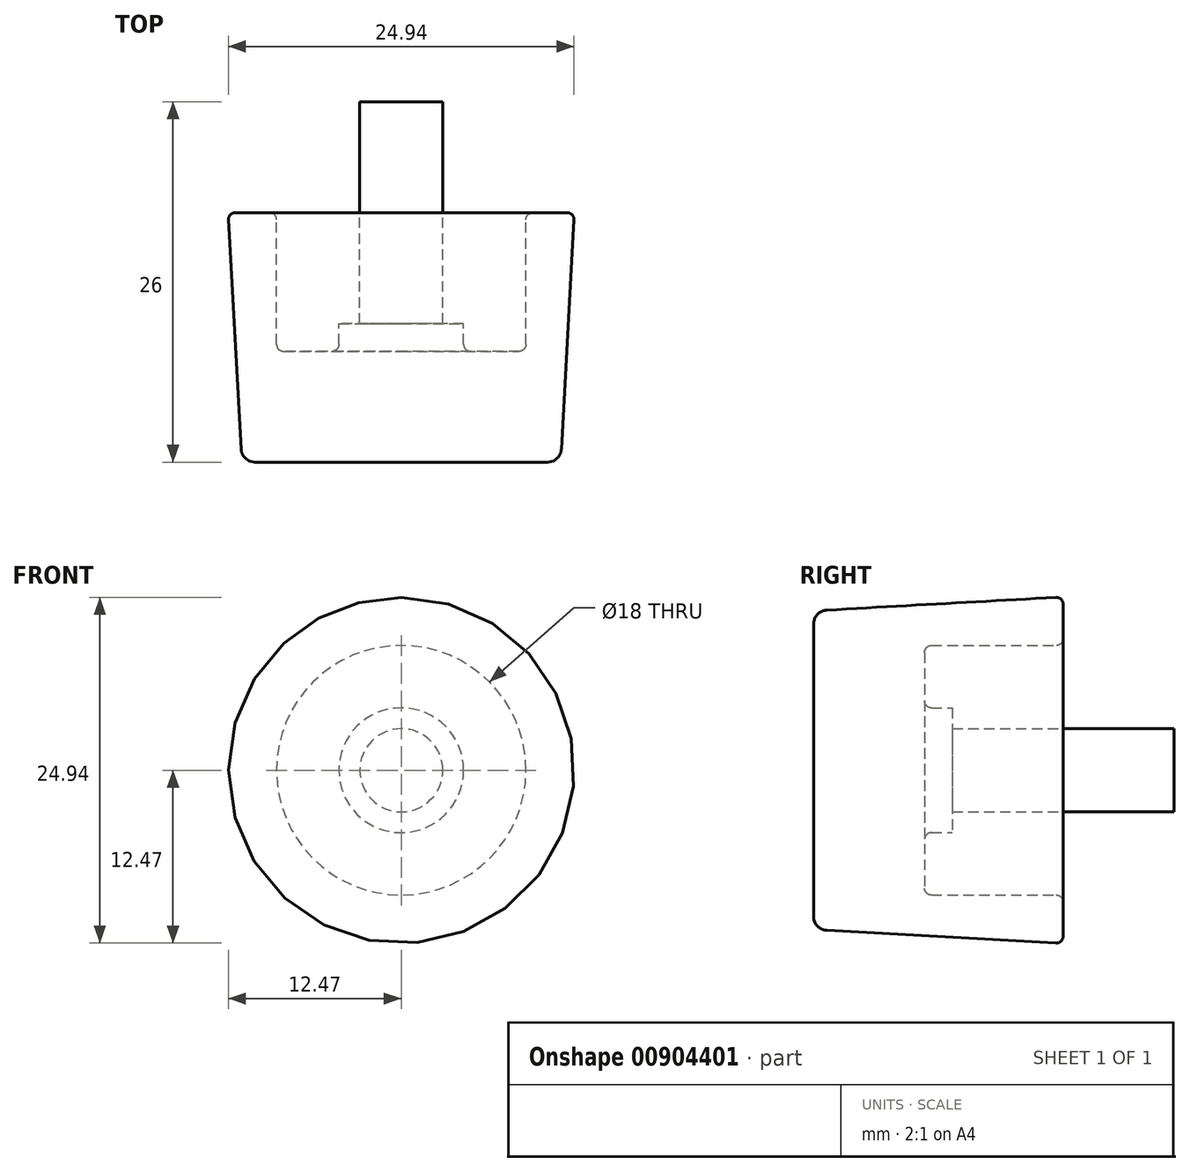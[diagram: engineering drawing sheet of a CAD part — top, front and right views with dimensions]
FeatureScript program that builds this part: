
annotation { "Feature Type Name" : "Feature", "Feature Type Description" : "" }
export const myFeature = defineFeature(function(context is Context, id is Id, definition is map)
    precondition{}
    {
        {
            var Q0;
            Q0=qCreatedBy(makeId("Top.planeOp"),FACE);
            var sketch = newSketch(context, id + "F0", { "sketchPlane" : qUnion([Q0])});
            skLineSegment(sketch, "E0", {"start": v(0, -7.02) * mm, "end": v(10.55, -7.02) * mm});
            skLineSegment(sketch, "E1", {"start": v(11.55, -6.07) * mm, "end": v(12.47, 10.45) * mm});
            skLineSegment(sketch, "E2", {"start": v(9, 10.48) * mm, "end": v(9, 1.48) * mm});
            skLineSegment(sketch, "E3", {"start": v(8.5, 0.98) * mm, "end": v(5, 0.98) * mm});
            skLineSegment(sketch, "E4", {"start": v(4.5, 1.48) * mm, "end": v(4.5, 2.98) * mm});
            skLineSegment(sketch, "E5", {"start": v(4.5, 2.98) * mm, "end": v(3, 2.98) * mm});
            skLineSegment(sketch, "E6", {"start": v(3, 2.98) * mm, "end": v(3, 18.98) * mm});
            skLineSegment(sketch, "E7", {"start": v(3, 18.98) * mm, "end": v(0, 18.98) * mm});
            skLineSegment(sketch, "E8", {"start": v(0, 18.98) * mm, "end": v(0, -7.02) * mm});
            skLineSegment(sketch, "E9", {"start": v(9.5, 10.98) * mm, "end": v(11.97, 10.98) * mm});
            skPoint(sketch, "E10.visualSharp", {"position": v(4.5, 0.98) * mm});
            skArc(sketch, "E10.filletArc", {"start": v(4.5, 1.48) * mm, "mid": v(4.65, 1.13) * mm, "end": v(5, 0.98) * mm});
            skPoint(sketch, "E11.visualSharp", {"position": v(9, 0.98) * mm});
            skArc(sketch, "E11.filletArc", {"start": v(8.5, 0.98) * mm, "mid": v(8.85, 1.13) * mm, "end": v(9, 1.48) * mm});
            skPoint(sketch, "E12.visualSharp", {"position": v(12.5, 10.98) * mm});
            skArc(sketch, "E12.filletArc", {"start": v(12.47, 10.45) * mm, "mid": v(12.33, 10.82) * mm, "end": v(11.97, 10.98) * mm});
            skPoint(sketch, "E13.visualSharp", {"position": v(9, 10.98) * mm});
            skPoint(sketch, "E14.visualSharp", {"position": v(11.5, -7.02) * mm});
            skArc(sketch, "E15.filletArc", {"start": v(9.5, 10.98) * mm, "mid": v(9.15, 10.83) * mm, "end": v(9, 10.48) * mm});
            skArc(sketch, "E16.filletArc", {"start": v(10.55, -7.02) * mm, "mid": v(11.24, -6.75) * mm, "end": v(11.55, -6.07) * mm});
            skSolve(sketch);
        }
        {
            var Q0;
            Q0 = qSketchRegion(id + "F0", true);
            var Q1;
            Q1=sQuery(id+"F0.wireOp",EDGE,"E8");
            revolve(context, id + "F1", {"surfaceOperationType" : NewSurfaceOperationType.NEW, "entities" : qUnion([Q0]), "axis" : qUnion([Q1]), "revolveType" : RevolveType.FULL});
        }
    });
